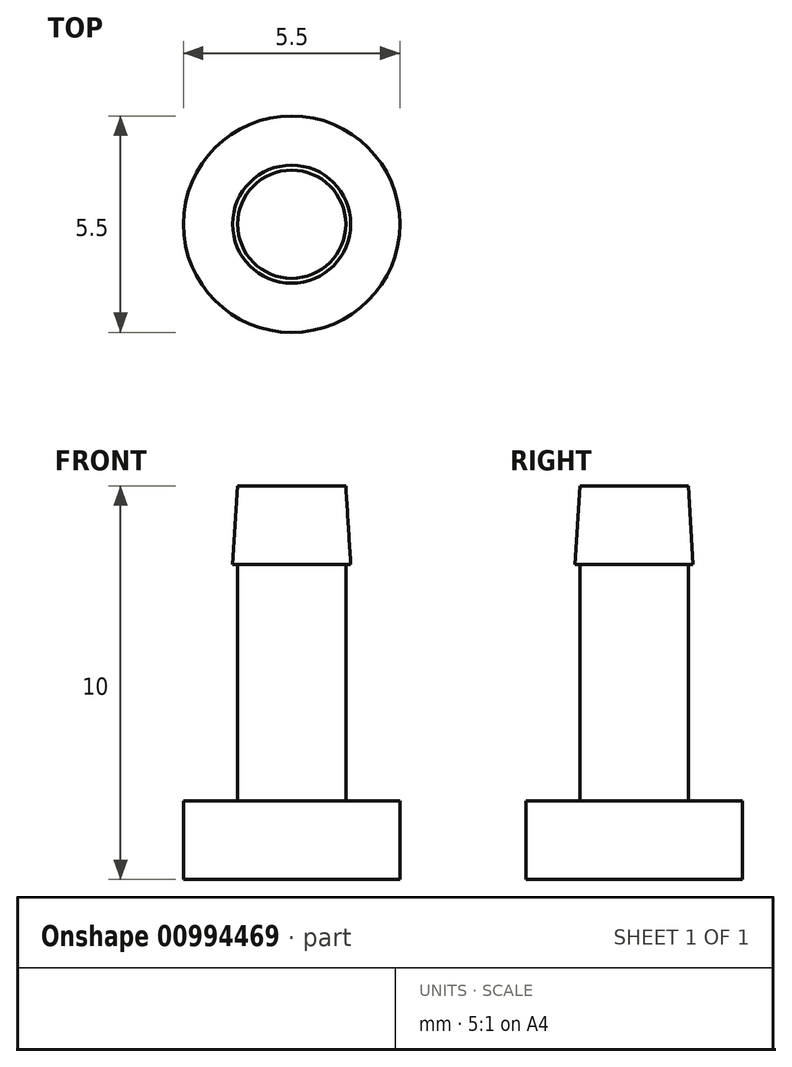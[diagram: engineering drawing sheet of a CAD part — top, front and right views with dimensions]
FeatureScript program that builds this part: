
annotation { "Feature Type Name" : "Feature", "Feature Type Description" : "" }
export const myFeature = defineFeature(function(context is Context, id is Id, definition is map)
    precondition{}
    {
        {
            var Q0;
            Q0=qCreatedBy(makeId("Top.planeOp"),FACE);
            var sketch = newSketch(context, id + "F0", { "sketchPlane" : qUnion([Q0])});
            skCircle(sketch, "E0", {"center": v(0, 0) * mm, "radius": 2.75 * mm});
            skCircle(sketch, "E1", {"center": v(0, 0) * mm, "radius": 1.38 * mm});
            skSolve(sketch);
        }
        {
            var Q0;
            Q0 = qSketchRegion(id + "F0", true);
            var Q1;
            Q1=makeQuery(id+"F0.imprint","IMPRINT",FACE,{"disambiguationData":[TD([[makeQuery(id+"F0.imprint","IMPRINT",EDGE,{"derivedFrom":sQuery(id+"F0.wireOp",EDGE,"E1")}),1.0]])]});
            extrude(context, id + "F1", {"entities" : qUnion([Q0, Q1]), "depth" : 2 * mm, "offsetDistance" : 25 * mm});
        }
        {
            var Q0;
            Q0=makeQuery(id+"F0.imprint","IMPRINT",FACE,{"disambiguationData":[TD([[makeQuery(id+"F0.imprint","IMPRINT",EDGE,{"derivedFrom":sQuery(id+"F0.wireOp",EDGE,"E1")}),1.0]])]});
            extrude(context, id + "F2", {"entities" : qUnion([Q0]), "operationType" : NewBodyOperationType.ADD, "depth" : 10 * mm, "offsetDistance" : 25 * mm});
        }
        {
            var Q0;
            Q0=makeQuery(id+"F2.opExtrude","CAP_FACE",FACE,{"disambiguationData":[OSD([sQuery(id+"F0.wireOp",EDGE,"E1")])],"isStart":false});
            cPlane(context, id + "F3", {"entities" : qUnion([Q0]), "cplaneType" : CPlaneType.OFFSET, "offset" : 2 * mm, "oppositeDirection" : true, "width" : 150 * mm, "height" : 150 * mm});
        }
        {
            var Q0;
            Q0=qCreatedBy(id+"F3.planeOp",FACE);
            var sketch = newSketch(context, id + "F4", { "sketchPlane" : qUnion([Q0])});
            skCircle(sketch, "E2", {"center": v(0, 0) * mm, "radius": 1.5 * mm});
            skSolve(sketch);
        }
        {
            var Q1;
            Q1=makeQuery(id+"F4.imprint","IMPRINT",FACE,{"disambiguationData":[TD([[makeQuery(id+"F4.imprint","IMPRINT",EDGE,{"derivedFrom":sQuery(id+"F4.wireOp",EDGE,"E2")}),1.0]])]});
            var Q2;
            Q2=makeQuery(id+"F2.opExtrude","CAP_FACE",FACE,{"disambiguationData":[OSD([sQuery(id+"F0.wireOp",EDGE,"E1")])],"isStart":false});
            loft(context, id + "F5", {"operationType" : NewBodyOperationType.ADD, "sheetProfilesArray" : [{ "sheetProfileEntities" : qUnion([Q1]) }, { "sheetProfileEntities" : qUnion([Q2]) }]});
        }
    });
